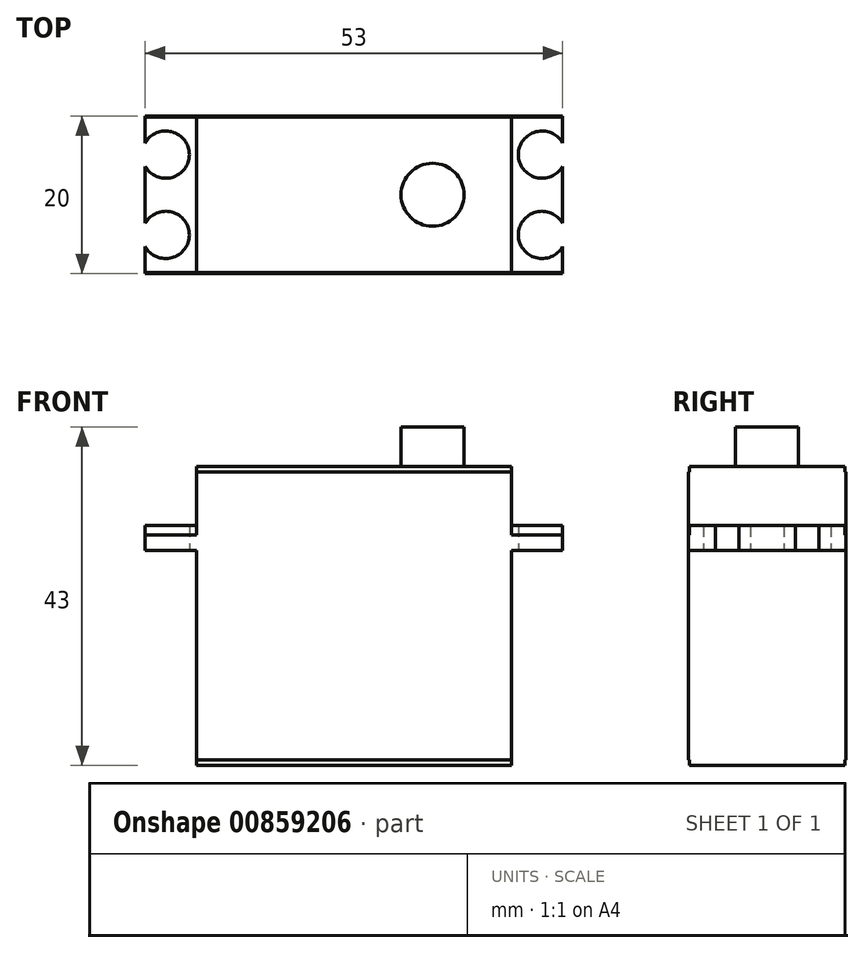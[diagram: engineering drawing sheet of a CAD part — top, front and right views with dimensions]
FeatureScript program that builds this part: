
annotation { "Feature Type Name" : "Feature", "Feature Type Description" : "" }
export const myFeature = defineFeature(function(context is Context, id is Id, definition is map)
    precondition{}
    {
        {
            var Q0;
            Q0=qCreatedBy(makeId("Front.planeOp"),FACE);
            var sketch = newSketch(context, id + "F0", { "sketchPlane" : qUnion([Q0])});
            skLineSegment(sketch, "E0.bottom", {"start": v(20, -18.3) * mm, "end": v(-20, -18.3) * mm});
            skLineSegment(sketch, "E0.top", {"start": v(20, 18.3) * mm, "end": v(-20, 18.3) * mm});
            skLineSegment(sketch, "E0.left", {"start": v(20, -18.3) * mm, "end": v(20, 8.3) * mm});
            skLineSegment(sketch, "E0.right", {"start": v(-20, -18.3) * mm, "end": v(-20, 8.3) * mm});
            skPoint(sketch, "E0.middle", {"position": v(0, 0) * mm});
            skLineSegment(sketch, "E1", {"start": v(20, 8.3) * mm, "end": v(26.5, 8.3) * mm});
            skLineSegment(sketch, "E2", {"start": v(26.5, 8.3) * mm, "end": v(26.5, 10.3) * mm});
            skLineSegment(sketch, "E3", {"start": v(26.5, 10.3) * mm, "end": v(20, 10.3) * mm});
            skLineSegment(sketch, "E4", {"start": v(-26.5, 10.3) * mm, "end": v(-26.5, 8.3) * mm});
            skLineSegment(sketch, "E5", {"start": v(-26.5, 8.3) * mm, "end": v(-20, 8.3) * mm});
            skLineSegment(sketch, "E6.trimOffspring", {"start": v(-20, 10.3) * mm, "end": v(-26.5, 10.3) * mm});
            skLineSegment(sketch, "E7.trimOffspring", {"start": v(-20, 10.3) * mm, "end": v(-20, 18.3) * mm});
            skLineSegment(sketch, "E8.trimOffspring", {"start": v(20, 10.3) * mm, "end": v(20, 18.3) * mm});
            skLineSegment(sketch, "E9", {"start": v(0, 0) * mm, "end": v(0, -24.51) * mm, "construction": true});
            skSolve(sketch);
        }
        {
            var Q0;
            Q0=qCreatedBy(makeId("Front.planeOp"),FACE);
            var sketch = newSketch(context, id + "F1", { "sketchPlane" : qUnion([Q0])});
            skLineSegment(sketch, "E10.bottom", {"start": v(20, -19) * mm, "end": v(-20, -19) * mm});
            skLineSegment(sketch, "E10.top", {"start": v(20, 19) * mm, "end": v(-20, 19) * mm});
            skLineSegment(sketch, "E10.left", {"start": v(20, -19) * mm, "end": v(20, 9) * mm});
            skLineSegment(sketch, "E10.right", {"start": v(-20, -19) * mm, "end": v(-20, 9) * mm});
            skPoint(sketch, "E10.middle", {"position": v(0, 0) * mm});
            skLineSegment(sketch, "E11", {"start": v(20, 9) * mm, "end": v(26.5, 9) * mm});
            skLineSegment(sketch, "E12", {"start": v(26.5, 9) * mm, "end": v(26.5, 11.5) * mm});
            skLineSegment(sketch, "E13", {"start": v(26.5, 11.5) * mm, "end": v(20, 11.5) * mm});
            skLineSegment(sketch, "E14", {"start": v(-26.5, 11.5) * mm, "end": v(-26.5, 9) * mm});
            skLineSegment(sketch, "E15", {"start": v(-26.5, 9) * mm, "end": v(-20, 9) * mm});
            skLineSegment(sketch, "E16.trimOffspring", {"start": v(-20, 11.5) * mm, "end": v(-26.5, 11.5) * mm});
            skLineSegment(sketch, "E17.trimOffspring", {"start": v(-20, 11.5) * mm, "end": v(-20, 19) * mm});
            skLineSegment(sketch, "E18.trimOffspring", {"start": v(20, 11.5) * mm, "end": v(20, 19) * mm});
            skLineSegment(sketch, "E19", {"start": v(0, 0) * mm, "end": v(0, -28.95) * mm, "construction": true});
            skSolve(sketch);
        }
        {
            var Q0;
            Q0 = qSketchRegion(id + "F1", true);
            extrude(context, id + "F2", {"entities" : qUnion([Q0]), "endBound" : BoundingType.SYMMETRIC, "depth" : 19.8 * mm, "offsetDistance" : 25 * mm});
        }
        {
            var Q0;
            Q0 = qSketchRegion(id + "F0", true);
            extrude(context, id + "F3", {"entities" : qUnion([Q0]), "endBound" : BoundingType.SYMMETRIC, "depth" : 20 * mm, "offsetDistance" : 25 * mm});
        }
        {
            var Q0;
            Q0=makeQuery(id+"F2.opExtrude","SWEPT_FACE",FACE,{"disambiguationData":[OSD([sQuery(id+"F1.wireOp",EDGE,"E10.top")])]});
            var sketch = newSketch(context, id + "F4", { "sketchPlane" : qUnion([Q0])});
            skCircle(sketch, "E20", {"center": v(10, 0) * mm, "radius": 4 * mm});
            skLineSegment(sketch, "E21", {"start": v(20, 0) * mm, "end": v(10, 0) * mm, "construction": true});
            skSolve(sketch);
        }
        {
            var Q0;
            Q0 = qSketchRegion(id + "F4", true);
            extrude(context, id + "F5", {"entities" : qUnion([Q0]), "operationType" : NewBodyOperationType.ADD, "depth" : 5 * mm, "offsetDistance" : 25 * mm});
        }
        {
            var Q0;
            Q0=makeQuery(id+"F3.opExtrude","SWEPT_FACE",FACE,{"disambiguationData":[OSD([sQuery(id+"F0.wireOp",EDGE,"E0.top")])]});
            var sketch = newSketch(context, id + "F6", { "sketchPlane" : qUnion([Q0])});
            skCircle(sketch, "E22", {"center": v(10, 0) * mm, "radius": 4 * mm});
            skSolve(sketch);
        }
        {
            var Q0;
            Q0 = qSketchRegion(id + "F6", true);
            extrude(context, id + "F7", {"entities" : qUnion([Q0]), "operationType" : NewBodyOperationType.ADD, "depth" : 5 * mm, "offsetDistance" : 25 * mm});
        }
        {
            var Q0;
            Q0=qCreatedBy(makeId("Top.planeOp"),FACE);
            var sketch = newSketch(context, id + "F8", { "sketchPlane" : qUnion([Q0])});
            skLineSegment(sketch, "E23.bottom", {"start": v(23.9, 5.1) * mm, "end": v(-23.9, 5.1) * mm, "construction": true});
            skLineSegment(sketch, "E23.top", {"start": v(23.9, -5.1) * mm, "end": v(-23.9, -5.1) * mm, "construction": true});
            skLineSegment(sketch, "E23.left", {"start": v(23.9, 5.1) * mm, "end": v(23.9, -5.1) * mm, "construction": true});
            skLineSegment(sketch, "E23.right", {"start": v(-23.9, 5.1) * mm, "end": v(-23.9, -5.1) * mm, "construction": true});
            skPoint(sketch, "E23.middle", {"position": v(0, 0) * mm});
            skPoint(sketch, "E24", {"position": v(23.9, 5.1) * mm});
            skPoint(sketch, "E25", {"position": v(23.9, -5.1) * mm});
            skPoint(sketch, "E26", {"position": v(-23.9, -5.1) * mm});
            skPoint(sketch, "E27", {"position": v(-23.9, 5.1) * mm});
            skSolve(sketch);
        }
        {
            var Q0;
            Q0=sQuery(id+"F8.wireOp",VERTEX,"E26");
            var Q1;
            Q1=sQuery(id+"F8.wireOp",VERTEX,"E25");
            var Q2;
            Q2=sQuery(id+"F8.wireOp",VERTEX,"E24");
            var Q3;
            Q3=sQuery(id+"F8.wireOp",VERTEX,"E27");
            var Q4;
            Q4=makeQuery(id+"F2.opExtrude","SWEPT_BODY",BODY,{"disambiguationData":[OSD([sQuery(id+"F1.wireOp",EDGE,"E10.bottom"),sQuery(id+"F1.wireOp",EDGE,"E10.top"),sQuery(id+"F1.wireOp",EDGE,"E10.left"),sQuery(id+"F1.wireOp",EDGE,"E10.right"),sQuery(id+"F1.wireOp",EDGE,"E11"),sQuery(id+"F1.wireOp",EDGE,"E12"),sQuery(id+"F1.wireOp",EDGE,"E13"),sQuery(id+"F1.wireOp",EDGE,"E14"),sQuery(id+"F1.wireOp",EDGE,"E15"),sQuery(id+"F1.wireOp",EDGE,"E16.trimOffspring"),sQuery(id+"F1.wireOp",EDGE,"E17.trimOffspring"),sQuery(id+"F1.wireOp",EDGE,"E18.trimOffspring")])]});
            var Q5;
            Q5=makeQuery(id+"F3.opExtrude","SWEPT_BODY",BODY,{"disambiguationData":[OSD([sQuery(id+"F0.wireOp",EDGE,"E0.bottom"),sQuery(id+"F0.wireOp",EDGE,"E0.top"),sQuery(id+"F0.wireOp",EDGE,"E0.left"),sQuery(id+"F0.wireOp",EDGE,"E0.right"),sQuery(id+"F0.wireOp",EDGE,"E1"),sQuery(id+"F0.wireOp",EDGE,"E2"),sQuery(id+"F0.wireOp",EDGE,"E3"),sQuery(id+"F0.wireOp",EDGE,"E4"),sQuery(id+"F0.wireOp",EDGE,"E5"),sQuery(id+"F0.wireOp",EDGE,"E6.trimOffspring"),sQuery(id+"F0.wireOp",EDGE,"E7.trimOffspring"),sQuery(id+"F0.wireOp",EDGE,"E8.trimOffspring")])]});
            hole(context, id + "F9", {"style" : HoleStyle.SIMPLE, "endStyle" : HoleEndStyle.THROUGH, "oppositeDirection" : true, "holeDiameter" : 6 * mm, "majorDiameter" : 8 * mm, "isTappedThrough" : true, "tappedDepth" : 12 * mm, "tapClearance" : 3, "locations" : qUnion([Q0, Q1, Q2, Q3]), "scope" : qUnion([Q4, Q5])});
        }
    });
